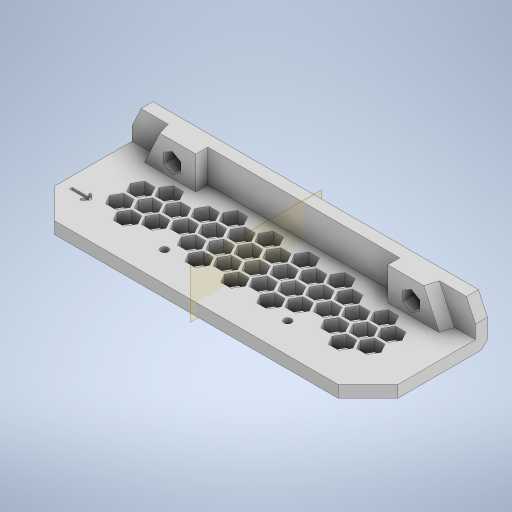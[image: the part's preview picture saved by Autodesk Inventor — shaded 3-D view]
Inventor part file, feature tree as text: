
AUTODESK INVENTOR PART (.ipt)
format: ipt  version: 2023 (Build 270158000, 158)  size: 1,077,248 bytes
history: native  units: mm
features: sketch x11, extrude x10, projected_geometry x9, chamfer x3, mirror x2, emboss x2, shell x1, pattern_linear x1, draft x1, plane x1
ambient origin geometry x8: Origin, YZ Plane, XZ Plane, XY Plane, X Axis, Y Axis, Z Axis, Center Point
bodies: Solid1 (feature_tree)
feature tree (41):
  extrude  "Extrusion1"  Depth=40.0mm
  chamfer  "Chamfer1"  Distance=15.0mm
  shell  "Shell1"  Thickness=4.0mm
  extrude  "Extrusion18"  Depth=40.0mm
  pattern_linear  "Rectangular Pattern4"  Spacing1=0.0mm  [1 undecoded]
  extrude  "Extrusion19"  Depth=0.5mm TaperAngle=45.0deg
  extrude  "Extrusion13"  Depth=1.0mm TaperAngle=0.0deg
  extrude  "Extrusion14"  Depth=10.0mm
  extrude  "Extrusion15"  Depth=2.5mm
  mirror  "Mirror4"
  extrude  "Extrusion4"  TaperAngle=0.0deg  [1 undecoded]
  extrude  "Extrusion5"  Depth=4.25mm
  sketch  "Sketch6"  dims[d23=0.0mm d24=0.0mm]
  extrude  "Extrusion6"  Depth=1.5mm TaperAngle=0.0deg
  draft  "FaceDraft2"
  extrude  "Extrusion7"  Depth=1.0mm
  chamfer  "Chamfer3"  Distance=36.859846mm
  mirror  "Mirror2"
  plane  "Work Plane1"
  chamfer  "Chamfer6"  Distance=7.0mm
  emboss  "Emboss2"
  emboss  "Emboss1"
  sketch  "Sketch1"  dims[d0=115.0mm d1=40.0mm d2=15.0mm d3=0.0mm d4=4.0mm]
  sketch  "Sketch4"  dims[d5=2.0mm d6=2.0mm d7=45.0deg d21=40.0mm]
  projected_geometry  "Projected Loop3"
  sketch  "Sketch5"  dims[d22=3.5mm]
  projected_geometry  "Projected Loop4"
  projected_geometry  "Projected Loop5"
  sketch  "Sketch12"  dims[d25=5.75mm]
  projected_geometry  "Projected Loop10"
  sketch  "Sketch17"  dims[d26=1.0mm d27=0.0mm]
  projected_geometry  "Projected Loop14"
  sketch  "Sketch19"  dims[d28=5.0mm]
  sketch  "Sketch20"  dims[d29=2.5mm]
  projected_geometry  "Projected Loop16"
  sketch  "Sketch23"  dims[d30=11.34464mm]
  projected_geometry  "Projected Loop19"
  sketch  "Sketch24"  dims[d31=4.0mm d32=0.0mm]
  projected_geometry  "Projected Loop20"
  sketch  "Sketch25"  dims[d33=15.0deg d34=0.0mm d35=0.0mm d36=0.5mm d37=2.0mm d38=45.0deg d53=1.0mm d54=0.0mm d71=10.0mm d73=2.5mm d74=0.0mm d75=0.0mm d77=4.25mm d78=1.5mm d79=0.0mm d80=1.0mm d81=-7.853982mm d89=36.859846mm d100=7.0mm d101=0.5mm d102=0.0mm d103=0.0mm d104=30.0mm d106=7.0mm d107=80.0mm d109=12.0mm d110=10.0mm d111=0.0mm d112=10.0mm d113=1.0mm d114=45.0deg d115=1.0mm d116=0.0mm]
  projected_geometry  "Projected Loop21"
note: 2 required parameter values undecoded (feature->parameter linkage not recoverable at this tier; creation-order binding heuristic only, values carry confidence <= 0.55)
